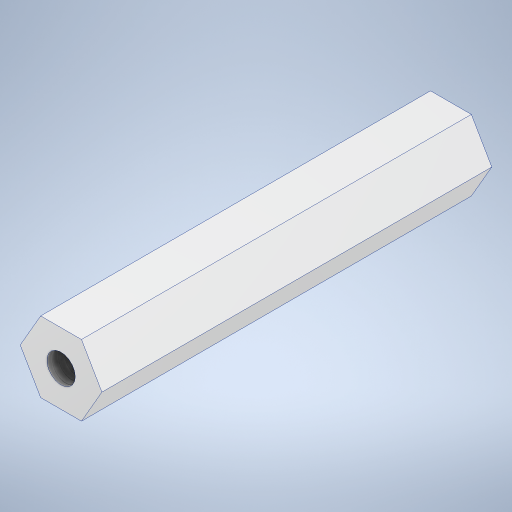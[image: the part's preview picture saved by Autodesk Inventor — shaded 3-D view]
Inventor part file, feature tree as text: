
AUTODESK INVENTOR PART (.ipt)
format: ipt  version: 2024 (Build 280153000, 153)  size: 226,304 bytes
history: native  units: in
note: dims shown in document units (in); Inventor stores cm internally (conversion verified against a paired STEP export)
features: extrude x1, thread x1, sketch x1
ambient origin geometry x8: Origin, YZ Plane, XZ Plane, XY Plane, X Axis, Y Axis, Z Axis, Center Point
bodies: Solid1 (feature_tree)
feature tree (3):
  extrude  "Extrusion1"  Depth=2.756in
  thread  "Thread1"  [1 undecoded]
  sketch  "Sketch1"  dims[d0=0.5in d1=0.201in d2=2.756in d3=0.0in d4=2.756in d5=0.0in]
note: 1 required parameter value undecoded (feature->parameter linkage not recoverable at this tier; creation-order binding heuristic only, values carry confidence <= 0.55)
